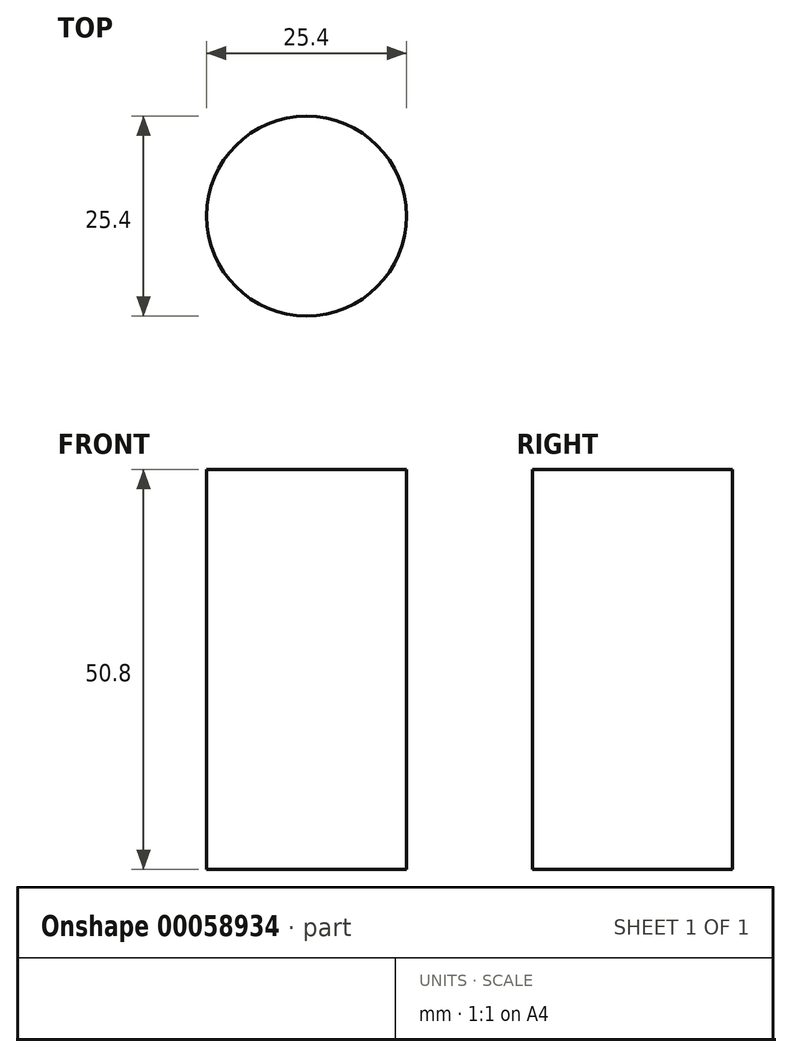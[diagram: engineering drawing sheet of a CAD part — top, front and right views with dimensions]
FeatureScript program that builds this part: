
annotation { "Feature Type Name" : "Feature", "Feature Type Description" : "" }
export const myFeature = defineFeature(function(context is Context, id is Id, definition is map)
    precondition{}
    {
        {
            var Q0;
            Q0=qCreatedBy(makeId("Top.planeOp"),FACE);
            var sketch = newSketch(context, id + "F0", { "sketchPlane" : qUnion([Q0])});
            skCircle(sketch, "E0", {"center": v(0, 0) * mm, "radius": 12.7 * mm});
            skSolve(sketch);
        }
        {
            var Q0;
            Q0=qSketchRegion(id+"F0",true);
            extrude(context, id + "F1", {"entities" : qUnion([Q0]), "depth" : 50.8 * mm});
        }
    });
